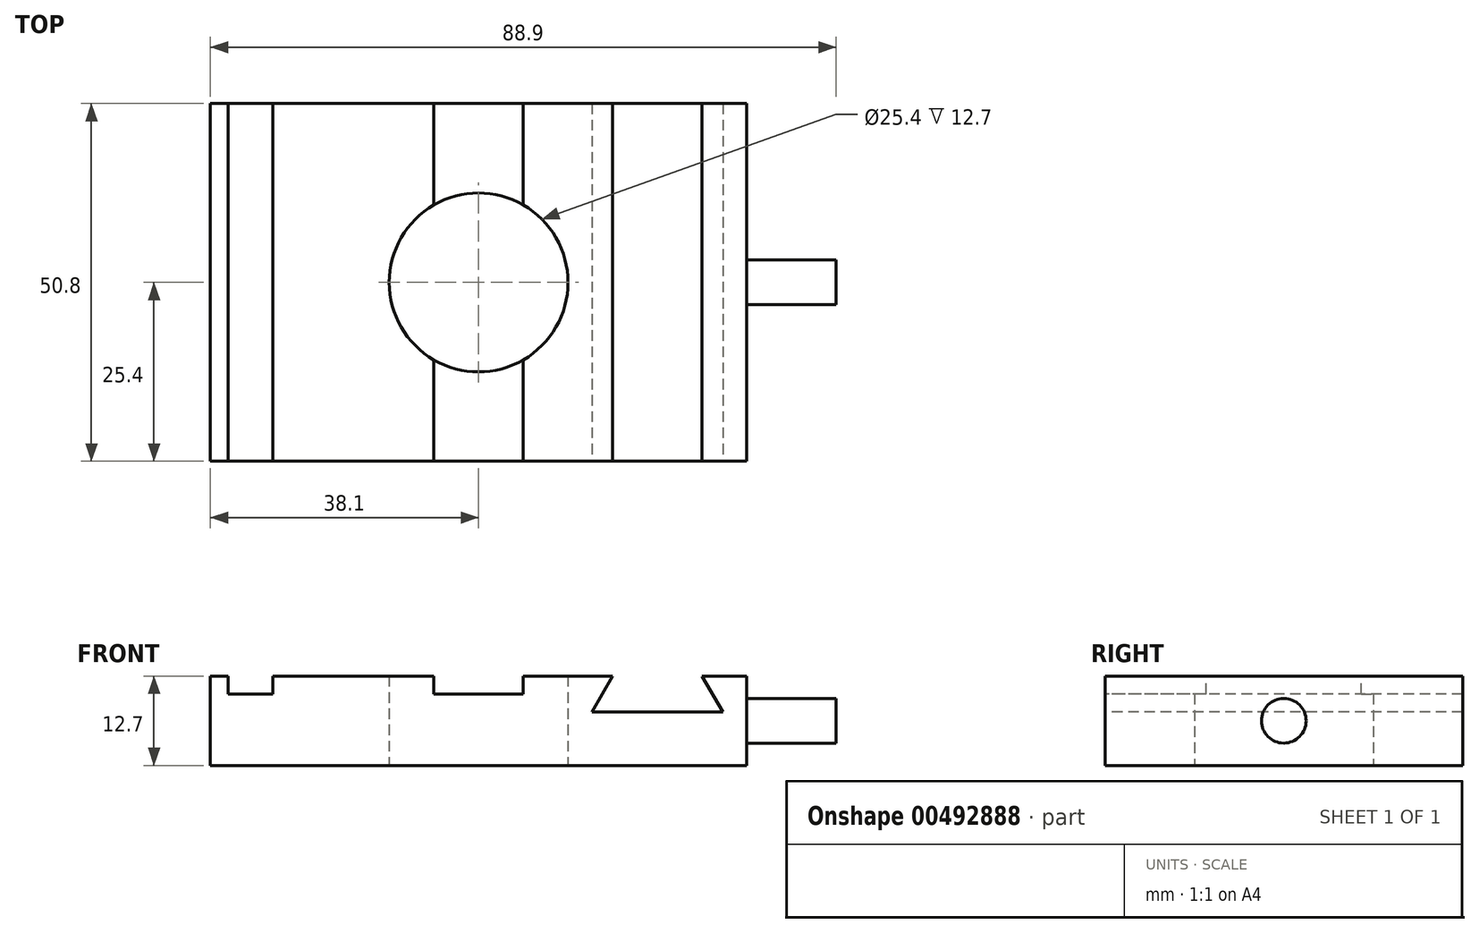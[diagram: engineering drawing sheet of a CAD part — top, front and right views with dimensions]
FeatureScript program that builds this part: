
annotation { "Feature Type Name" : "Feature", "Feature Type Description" : "" }
export const myFeature = defineFeature(function(context is Context, id is Id, definition is map)
    precondition{}
    {
        {
            var Q0;
            Q0=qCreatedBy(makeId("Top.planeOp"),FACE);
            var sketch = newSketch(context, id + "F0", { "sketchPlane" : qUnion([Q0])});
            skCircle(sketch, "E0", {"center": v(0, 0) * mm, "radius": 12.7 * mm});
            skLineSegment(sketch, "E1", {"start": v(-38.1, 25.4) * mm, "end": v(38.1, 25.4) * mm});
            skLineSegment(sketch, "E2", {"start": v(38.1, 25.4) * mm, "end": v(38.1, -25.4) * mm});
            skLineSegment(sketch, "E3", {"start": v(38.1, -25.4) * mm, "end": v(-38.1, -25.4) * mm});
            skLineSegment(sketch, "E4", {"start": v(-38.1, -25.4) * mm, "end": v(-38.1, 25.4) * mm});
            skSolve(sketch);
        }
        {
            var Q0;
            Q0=makeQuery(id+"F0.imprint","IMPRINT",FACE,{"disambiguationData":[TD([[makeQuery(id+"F0.imprint","IMPRINT",EDGE,{"derivedFrom":sQuery(id+"F0.wireOp",EDGE,"E0")}),-1.0]])]});
            extrude(context, id + "F1", {"entities" : qUnion([Q0]), "depth" : 12.7 * mm, "offsetDistance" : 25.4 * mm});
        }
        {
            var Q0;
            Q0=makeQuery(id+"F1.opExtrude","CAP_FACE",FACE,{"disambiguationData":[OSD([sQuery(id+"F0.wireOp",EDGE,"E0"),sQuery(id+"F0.wireOp",EDGE,"E1"),sQuery(id+"F0.wireOp",EDGE,"E2"),sQuery(id+"F0.wireOp",EDGE,"E3"),sQuery(id+"F0.wireOp",EDGE,"E4")])],"isStart":false});
            var sketch = newSketch(context, id + "F2", { "sketchPlane" : qUnion([Q0])});
            skLineSegment(sketch, "E5.bottom", {"start": v(-35.56, 25.4) * mm, "end": v(-29.2, 25.4) * mm});
            skLineSegment(sketch, "E5.top", {"start": v(-35.56, -25.4) * mm, "end": v(-29.2, -25.4) * mm});
            skLineSegment(sketch, "E5.left", {"start": v(-35.56, 25.4) * mm, "end": v(-35.56, -25.4) * mm});
            skLineSegment(sketch, "E5.right", {"start": v(-29.2, 25.4) * mm, "end": v(-29.2, -25.4) * mm});
            skLineSegment(sketch, "E6", {"start": v(-6.35, 25.4) * mm, "end": v(-6.35, -25.4) * mm});
            skLineSegment(sketch, "E7", {"start": v(-6.35, -25.4) * mm, "end": v(6.35, -25.4) * mm});
            skLineSegment(sketch, "E8", {"start": v(6.35, -25.4) * mm, "end": v(6.35, 25.4) * mm});
            skLineSegment(sketch, "E9", {"start": v(6.35, 25.4) * mm, "end": v(-6.35, 25.4) * mm});
            skPoint(sketch, "E10", {"position": v(0, 0) * mm});
            skLineSegment(sketch, "E11", {"start": v(0, 25.4) * mm, "end": v(0, -25.4) * mm, "construction": true});
            skSolve(sketch);
        }
        {
            var Q0;
            Q0=makeQuery(id+"F2.imprint","IMPRINT",FACE,{"disambiguationData":[TD([[makeQuery(id+"F2.imprint","IMPRINT",EDGE,{"derivedFrom":sQuery(id+"F2.wireOp",EDGE,"E5.bottom")}),-1.0]])]});
            var Q1;
            {var subQ0=sQuery(id+"F2.wireOp",EDGE,"E9");Q1=makeQuery(id+"F2.imprint","IMPRINT",FACE,{"disambiguationData":[TD([[makeQuery(id+"F2.imprint","IMPRINT",EDGE,{"derivedFrom":subQ0}),-1.0]])]});}
            var Q2;
            {var subQ0=sQuery(id+"F2.wireOp",EDGE,"E7");Q2=makeQuery(id+"F2.imprint","IMPRINT",FACE,{"disambiguationData":[TD([[makeQuery(id+"F2.imprint","IMPRINT",EDGE,{"derivedFrom":subQ0}),-1.0]])]});}
            extrude(context, id + "F3", {"entities" : qUnion([Q0, Q1, Q2]), "operationType" : NewBodyOperationType.REMOVE, "oppositeDirection" : true, "depth" : 2.54 * mm, "offsetDistance" : 25.4 * mm});
        }
        {
            var Q0;
            Q0=makeQuery(id+"F1.opExtrude","SWEPT_FACE",FACE,{"disambiguationData":[OSD([sQuery(id+"F0.wireOp",EDGE,"E3")])]});
            var sketch = newSketch(context, id + "F4", { "sketchPlane" : qUnion([Q0])});
            skLineSegment(sketch, "E12", {"start": v(19.05, 12.7) * mm, "end": v(16.12, 7.62) * mm});
            skLineSegment(sketch, "E13", {"start": v(16.12, 7.62) * mm, "end": v(34.68, 7.62) * mm});
            skLineSegment(sketch, "E14", {"start": v(34.68, 7.62) * mm, "end": v(31.75, 12.7) * mm});
            skLineSegment(sketch, "E15", {"start": v(31.75, 12.7) * mm, "end": v(19.05, 12.7) * mm});
            skLineSegment(sketch, "E16", {"start": v(25.4, 7.62) * mm, "end": v(25.4, 12.7) * mm, "construction": true});
            skSolve(sketch);
        }
        {
            var Q0;
            Q0 = qSketchRegion(id + "F4", true);
            extrude(context, id + "F5", {"entities" : qUnion([Q0]), "operationType" : NewBodyOperationType.REMOVE, "endBound" : BoundingType.UP_TO_NEXT, "oppositeDirection" : true, "depth" : 25.4 * mm, "offsetDistance" : 25.4 * mm});
        }
        {
            var Q0;
            Q0=makeQuery(id+"F1.opExtrude","SWEPT_FACE",FACE,{"disambiguationData":[OSD([sQuery(id+"F0.wireOp",EDGE,"E2")])]});
            var sketch = newSketch(context, id + "F6", { "sketchPlane" : qUnion([Q0])});
            skCircle(sketch, "E17", {"center": v(0, 6.35) * mm, "radius": 3.18 * mm});
            skPoint(sketch, "E17.centerSnap0", {"position": v(25.4, 6.35) * mm});
            skPoint(sketch, "E17.centerSnap1", {"position": v(0, 0) * mm});
            skSolve(sketch);
        }
        {
            var Q0;
            Q0=makeQuery(id+"F6.imprint","IMPRINT",FACE,{"disambiguationData":[TD([[makeQuery(id+"F6.imprint","IMPRINT",EDGE,{"derivedFrom":sQuery(id+"F6.wireOp",EDGE,"E17")}),1.0]])]});
            extrude(context, id + "F7", {"entities" : qUnion([Q0]), "operationType" : NewBodyOperationType.ADD, "depth" : 12.7 * mm, "offsetDistance" : 25.4 * mm});
        }
    });
